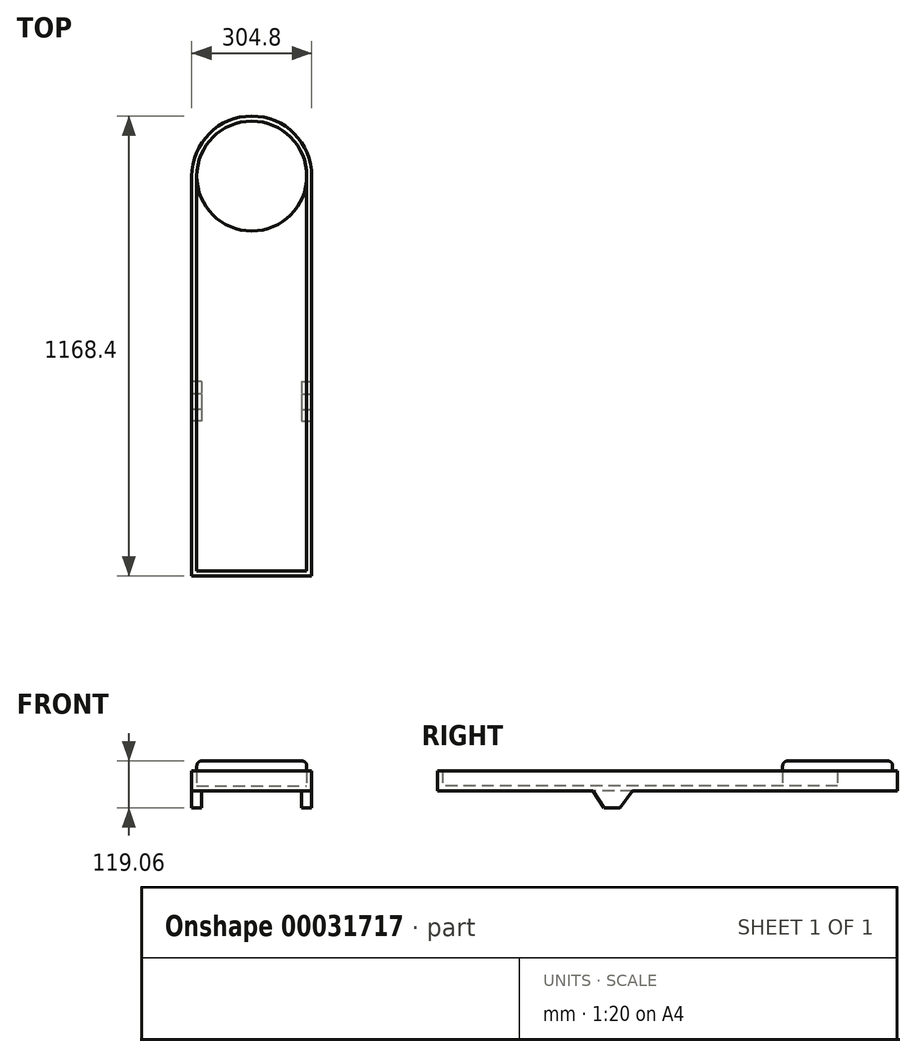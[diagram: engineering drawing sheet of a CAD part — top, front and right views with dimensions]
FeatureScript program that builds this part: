
annotation { "Feature Type Name" : "Feature", "Feature Type Description" : "" }
export const myFeature = defineFeature(function(context is Context, id is Id, definition is map)
    precondition{}
    {
        {
            var Q0;
            Q0=qCreatedBy(makeId("Top.planeOp"),FACE);
            var sketch = newSketch(context, id + "F0", { "sketchPlane" : qUnion([Q0])});
            skCircle(sketch, "E0", {"center": v(0, 0) * mm, "radius": 152.4 * mm});
            skLineSegment(sketch, "E1.bottom", {"start": v(-152.4, 0) * mm, "end": v(152.4, 0) * mm});
            skLineSegment(sketch, "E1.top", {"start": v(-152.4, -1016) * mm, "end": v(152.4, -1016) * mm});
            skLineSegment(sketch, "E1.left", {"start": v(-152.4, 0) * mm, "end": v(-152.4, -1016) * mm});
            skLineSegment(sketch, "E1.right", {"start": v(152.4, 0) * mm, "end": v(152.4, -1016) * mm});
            skSolve(sketch);
        }
        {
            var Q0;
            Q0=makeQuery(id+"F0.imprint","IMPRINT",FACE,{"disambiguationData":[TD([[makeQuery(id+"F0.imprint","IMPRINT",EDGE,{"derivedFrom":sQuery(id+"F0.wireOp",EDGE,"E1.top")}),1.0]])]});
            var Q1;
            {var subQ0=sQuery(id+"F0.wireOp",EDGE,"E1.bottom");Q1=makeQuery(id+"F0.imprint","IMPRINT",FACE,{"disambiguationData":[TD([[makeQuery(id+"F0.imprint","IMPRINT",EDGE,{"derivedFrom":subQ0}),-1.0]])]});}
            var Q2;
            {var subQ0=sQuery(id+"F0.wireOp",EDGE,"E1.bottom");Q2=makeQuery(id+"F0.imprint","IMPRINT",FACE,{"disambiguationData":[TD([[makeQuery(id+"F0.imprint","IMPRINT",EDGE,{"derivedFrom":subQ0}),1.0]])]});}
            extrude(context, id + "F1", {"entities" : qUnion([Q0, Q1, Q2]), "depth" : 50.8 * mm});
        }
        {
            var Q0;
            Q0=makeQuery(id+"F1.opExtrude","CAP_FACE",FACE,{"disambiguationData":[OSD([sQuery(id+"F0.wireOp",EDGE,"E0"),sQuery(id+"F0.wireOp",EDGE,"E1.top"),sQuery(id+"F0.wireOp",EDGE,"E1.left"),sQuery(id+"F0.wireOp",EDGE,"E1.right")])],"isStart":false});
            shell(context, id + "F2", {"entities" : qUnion([Q0]), "thickness" : 12.7 * mm});
        }
        {
            var Q0;
            Q0=makeQuery(id+"F2.opShell","OFFSET_FACE",FACE,{"disambiguationData":[OSD([sQuery(id+"F0.wireOp",EDGE,"E0"),sQuery(id+"F0.wireOp",EDGE,"E1.top"),sQuery(id+"F0.wireOp",EDGE,"E1.left"),sQuery(id+"F0.wireOp",EDGE,"E1.right")])]});
            var sketch = newSketch(context, id + "F3", { "sketchPlane" : qUnion([Q0])});
            skCircle(sketch, "E2", {"center": v(0, 0) * mm, "radius": 139.7 * mm});
            skSolve(sketch);
        }
        {
            var Q0;
            Q0 = qSketchRegion(id + "F3", true);
            var Q1;
            {var subQ0=sQuery(id+"F3.wireOp",EDGE,"E2");var subQ3=sQuery(id+"F0.wireOp",EDGE,"E1.left");var subQ4=makeQuery(id+"F3.imprint","INTERSECT",VERTEX,{"derivedFrom":[makeQuery(id+"F2.opShell","OFFSET_EDGE",EDGE,{"disambiguationData":[OSD([subQ3]),TDD([makeQuery(id+"F1.opExtrude","CAP_EDGE",EDGE,{"disambiguationData":[OSD([subQ3])],"isStart":true})])]}),subQ0]});Q1=makeQuery(id+"F3.imprint","IMPRINT",FACE,{"disambiguationData":[TD([[makeQuery(id+"F3.imprint","IMPRINT",EDGE,{"disambiguationData":[TD([[subQ4,1.0]])],"derivedFrom":subQ0}),1.0]])]});}
            extrude(context, id + "F4", {"entities" : qUnion([Q0, Q1]), "operationType" : NewBodyOperationType.ADD, "depth" : 63.5 * mm});
        }
        {
            var Q0;
            Q0=makeQuery(id+"F4.opExtrude","CAP_EDGE",EDGE,{"disambiguationData":[OSD([sQuery(id+"F3.wireOp",EDGE,"E2")])],"isStart":false});
            fillet(context, id + "F5", {"entities" : qUnion([Q0]), "radius" : 12.7 * mm, "tangentPropagation" : true, "allowEdgeOverflow" : false});
        }
        {
            var Q0;
            Q0=makeQuery(id+"F1.opExtrude","SWEPT_FACE",FACE,{"disambiguationData":[OSD([sQuery(id+"F0.wireOp",EDGE,"E1.left")])]});
            var sketch = newSketch(context, id + "F6", { "sketchPlane" : qUnion([Q0])});
            skLineSegment(sketch, "E3", {"start": v(521.64, 0) * mm, "end": v(553.32, -42.86) * mm});
            skLineSegment(sketch, "E4", {"start": v(553.32, -42.86) * mm, "end": v(593.44, -42.86) * mm});
            skLineSegment(sketch, "E5", {"start": v(593.44, -42.86) * mm, "end": v(621.95, 0) * mm});
            skLineSegment(sketch, "E6", {"start": v(521.64, 0) * mm, "end": v(621.95, 0) * mm});
            skSolve(sketch);
        }
        {
            var Q0;
            Q0 = qSketchRegion(id + "F6", true);
            extrude(context, id + "F7", {"entities" : qUnion([Q0]), "oppositeDirection" : true, "depth" : 25.4 * mm});
        }
        {
            var Q0;
            Q0=makeQuery(id+"F7.opExtrude","SWEPT_BODY",BODY,{"disambiguationData":[OSD([sQuery(id+"F6.wireOp",EDGE,"E3"),sQuery(id+"F6.wireOp",EDGE,"E4"),sQuery(id+"F6.wireOp",EDGE,"E5"),sQuery(id+"F6.wireOp",EDGE,"E6")])]});
            var Q1;
            Q1=qCreatedBy(makeId("Right.planeOp"),FACE);
            mirror(context, id + "F8", {"operationType" : NewBodyOperationType.ADD, "entities" : qUnion([Q0]), "mirrorPlane" : qUnion([Q1])});
        }
    });
